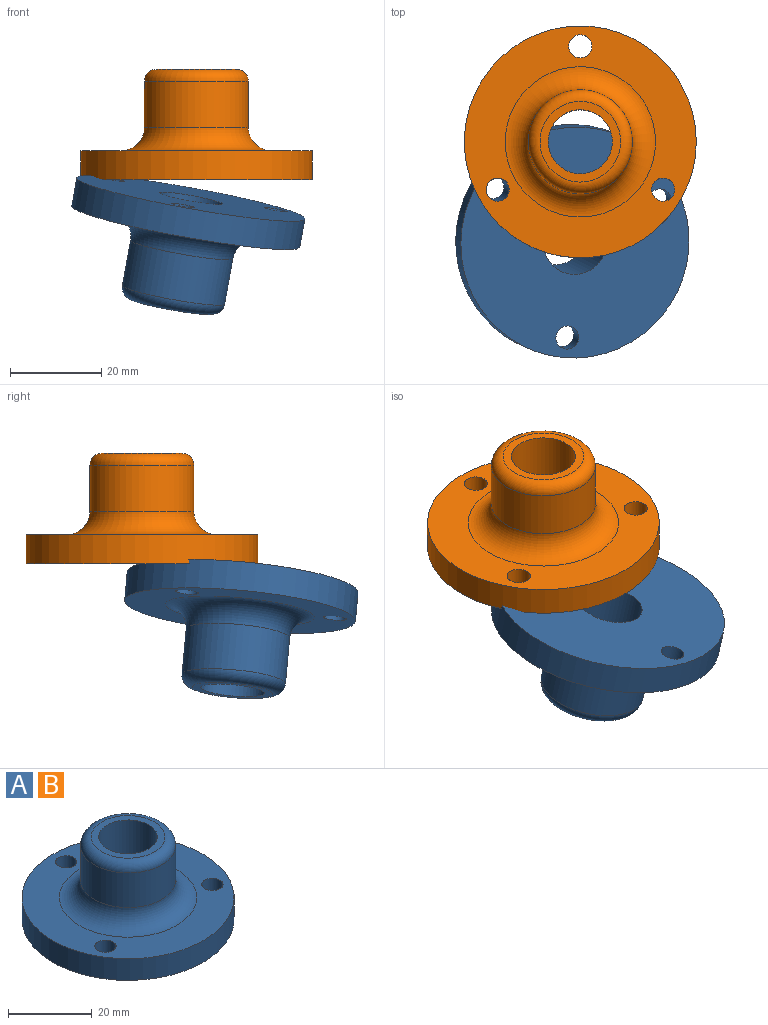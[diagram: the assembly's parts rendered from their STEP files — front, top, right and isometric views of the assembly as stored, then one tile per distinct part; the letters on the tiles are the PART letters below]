
ASSEMBLY  parts=2 mates=1
PART A: 11 faces, bbox 50.8x50.8x24.1 mm
  f0: cylinder r=25.4mm len=50.8mm, axis (0,0,-1), area 1013.4mm2, adj f1,f2
  f1: plane 50.8x50.8mm, normal (0,0,1), area 1114.5mm2, adj f0,f6,f8,f9,f10
  f2: plane 50.8x50.8mm, normal (0,0,-1), area 1811.6mm2, adj f0,f3,f8,f9,f10
  f3: cylinder r=7.01mm len=24.13mm, axis (0,0,-1), area 1062.9mm2, adj f2,f5
  f4: cylinder r=11.38mm len=22.77mm, axis (0,0,-1), area 726.7mm2, adj f6,f7
  f5: plane 17.69x17.69mm, normal (0,0,1), area 91.3mm2, adj f3,f7
  f6: torus R=16.46mm, axis (0,0,1), area 663.3mm2, adj f1,f4
  f7: torus R=8.84mm, axis (0,0,1), area 262.2mm2, adj f4,f5
  f8: cylinder r=2.54mm len=6.35mm, axis (0,0,1), area 101.3mm2, adj f1,f2
  f9: cylinder r=2.54mm len=6.35mm, axis (0,0,1), area 101.3mm2, adj f1,f2
  f10: cylinder r=2.54mm len=6.35mm, axis (0,0,1), area 101.3mm2, adj f1,f2
PART B: same geometry as A
PLACE A rot(axis=(-1,0.04,0.09),175.2deg) t=(13.94,-37.96,-1.38)mm
PLACE B t=(15.12,-15.92,2.72)mm fixed
MATE ball A.f9 <-> B.f9  axis (0.18,-0.09,0.98) through (-3,-26.38,2.72)mm
